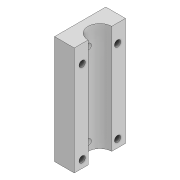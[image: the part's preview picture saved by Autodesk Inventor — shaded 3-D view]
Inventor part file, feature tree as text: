
AUTODESK INVENTOR PART (.ipt)
format: ipt  version: 2022 (Build 260153000, 153)  size: 143,360 bytes
history: native  units: mm
features: extrude x5, sketch x4, projected_geometry x1
ambient origin geometry x8: Origin, YZ Plane, XZ Plane, XY Plane, X Axis, Y Axis, Z Axis, Center Point
bodies: Solid1 (feature_tree)
feature tree (10):
  extrude  "Extrusion1"  Depth=10.0mm
  extrude  "Extrusion2"  Depth=10.0mm
  sketch  "Sketch3"  dims[d4=13.0mm d5=55.0mm d6=0.0mm]
  extrude  "Extrusion3"  Depth=55.0mm TaperAngle=0.0deg
  extrude  "Extrusion4"  Depth=6.0mm
  extrude  "Extrusion5"  Depth=6.0mm
  sketch  "Sketch1"  dims[d0=12.0mm d1=10.0mm]
  sketch  "Sketch2"  dims[d2=10.0mm d3=13.0mm]
  projected_geometry  "Projected Loop1"
  sketch  "Sketch5"  dims[d7=3.1mm d8=4.0mm d9=3.1mm d10=46.0mm d11=13.0mm d12=13.0mm d13=55.0mm d14=0.0mm d15=2.0mm d16=2.0mm d17=6.0mm d18=0.0mm d19=3.2mm d20=3.2mm d21=3.2mm d22=3.2mm d23=4.0mm d24=4.0mm d25=4.0mm d26=4.0mm d27=100.0mm d28=0.0mm d29=100.0mm d30=0.0mm]
